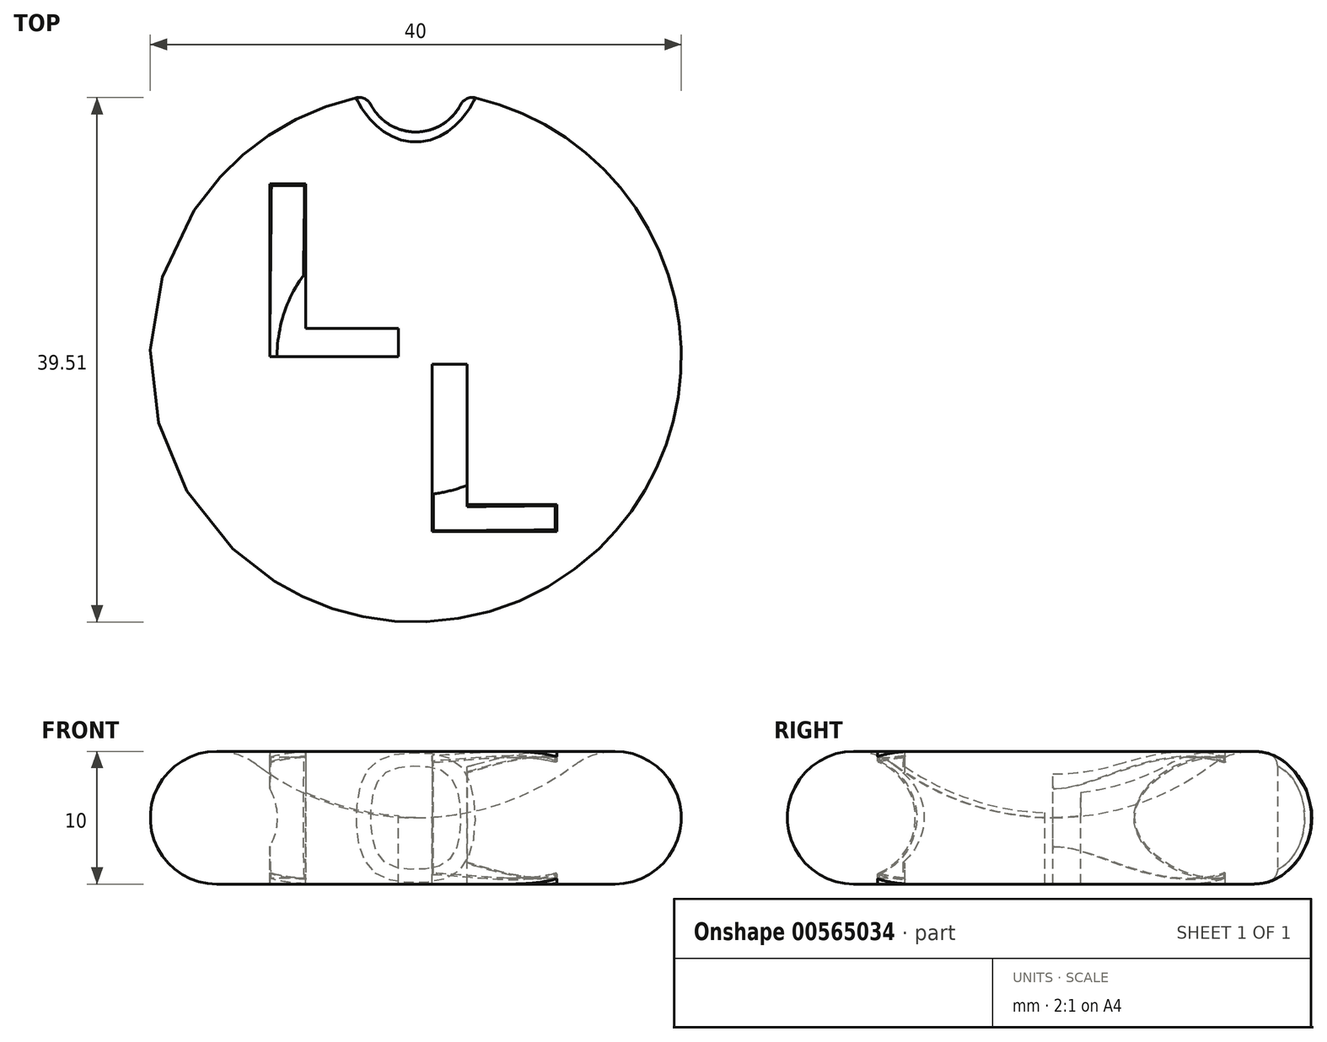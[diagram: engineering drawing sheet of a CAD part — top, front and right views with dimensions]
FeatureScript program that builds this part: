
annotation { "Feature Type Name" : "Feature", "Feature Type Description" : "" }
export const myFeature = defineFeature(function(context is Context, id is Id, definition is map)
    precondition{}
    {
        {
            var Q0;
            Q0=qCreatedBy(makeId("Front.planeOp"),FACE);
            var sketch = newSketch(context, id + "F0", { "sketchPlane" : qUnion([Q0])});
            skArc(sketch, "E0", {"start": v(-12, 9) * mm, "mid": v(-19.74, 6.58) * mm, "end": v(-15, 0) * mm});
            skArc(sketch, "E1", {"start": v(-12, 9) * mm, "mid": v(-6.32, 6.03) * mm, "end": v(0, 5) * mm});
            skLineSegment(sketch, "E2", {"start": v(0, 5) * mm, "end": v(0, 0) * mm});
            skLineSegment(sketch, "E3", {"start": v(0, 0) * mm, "end": v(-15, 0) * mm});
            skSolve(sketch);
        }
        {
            var Q0;
            Q0=makeQuery(id+"F0.imprint","IMPRINT",FACE,{"disambiguationData":[TD([[makeQuery(id+"F0.imprint","IMPRINT",EDGE,{"derivedFrom":sQuery(id+"F0.wireOp",EDGE,"E0")}),1.0]])]});
            var Q1;
            Q1=sQuery(id+"F0.wireOp",EDGE,"E2");
            revolve(context, id + "F1", {"entities" : qUnion([Q0]), "axis" : qUnion([Q1]), "revolveType" : RevolveType.FULL});
        }
        {
            var Q0;
            Q0=qCreatedBy(makeId("Top.planeOp"),FACE);
            cPlane(context, id + "F2", {"entities" : qUnion([Q0]), "cplaneType" : CPlaneType.OFFSET, "offset" : 10 * mm, "width" : 152.4 * mm, "height" : 152.4 * mm});
        }
        {
            var Q0;
            Q0=qCreatedBy(id+"F2.planeOp",FACE);
            var sketch = newSketch(context, id + "F3", { "sketchPlane" : qUnion([Q0])});
            skText(sketch, "E4", { "text": "L", "fontName": "Arimo-Bold.ttf"});
            skText(sketch, "E5", { "text": "L", "fontName": "Arimo-Bold.ttf"});
            const initialGuessF3  = {"E4": [-0.01226, 0, 1, 0, 0.0136], "E5": [0, -0.01319, 1, 0, 0.01319]};
            skSetInitialGuess(sketch, initialGuessF3);
            skSolve(sketch);
        }
        {
            var Q0;
            Q0=makeQuery(id+"F3.imprint","IMPRINT",FACE,{"disambiguationData":[TD([[makeQuery(id+"F3.imprint","IMPRINT",EDGE,{"derivedFrom":sQuery(id+"F3.wireOp",EDGE,"E5.sketch_text.stroke-0")}),-1.0]])]});
            var Q1;
            Q1=makeQuery(id+"F3.imprint","IMPRINT",FACE,{"disambiguationData":[TD([[makeQuery(id+"F3.imprint","IMPRINT",EDGE,{"derivedFrom":sQuery(id+"F3.wireOp",EDGE,"E4.sketch_text.stroke-0")}),-1.0]])]});
            extrude(context, id + "F4", {"entities" : qUnion([Q0, Q1]), "operationType" : NewBodyOperationType.REMOVE, "oppositeDirection" : true, "depth" : 25.4 * mm, "offsetDistance" : 25.4 * mm});
        }
        {
            var Q0;
            Q0=qCreatedBy(makeId("Front.planeOp"),FACE);
            var sketch = newSketch(context, id + "F5", { "sketchPlane" : qUnion([Q0])});
            skCircle(sketch, "E6", {"center": v(-15, 5) * mm, "radius": 4.56 * mm});
            skSolve(sketch);
        }
        {
            var Q0;
            Q0 = qSketchRegion(id + "F5", true);
            var Q1;
            Q1=sQuery(id+"F0.wireOp",EDGE,"E2");
            revolve(context, id + "F6", {"operationType" : NewBodyOperationType.ADD, "entities" : qUnion([Q0]), "axis" : qUnion([Q1]), "revolveType" : RevolveType.FULL});
        }
        {
            var Q0;
            Q0=qCreatedBy(makeId("Top.planeOp"),FACE);
            var sketch = newSketch(context, id + "F7", { "sketchPlane" : qUnion([Q0])});
            skCircle(sketch, "E7", {"center": v(0, 20.73) * mm, "radius": 3.8 * mm});
            skSolve(sketch);
        }
        {
            var Q0;
            Q0=makeQuery(id+"F7.imprint","IMPRINT",FACE,{"disambiguationData":[TD([[makeQuery(id+"F7.imprint","IMPRINT",EDGE,{"derivedFrom":sQuery(id+"F7.wireOp",EDGE,"E7")}),1.0]])]});
            extrude(context, id + "F8", {"entities" : qUnion([Q0]), "operationType" : NewBodyOperationType.REMOVE, "depth" : 25.4 * mm, "offsetDistance" : 25.4 * mm});
        }
        {
            var Q0;
            Q0=makeQuery(id+"F8.boolean.opBoolean","INTERSECT",EDGE,{"derivedFrom":[makeQuery(id+"F1.opRevolve","SWEPT_FACE",FACE,{"disambiguationData":[OSD([sQuery(id+"F0.wireOp",EDGE,"E0")])]}),makeQuery(id+"F8.opExtrude","SWEPT_FACE",FACE,{"disambiguationData":[OSD([sQuery(id+"F7.wireOp",EDGE,"E7")])]})]});
            fillet(context, id + "F9", {"entities" : qUnion([Q0]), "radius" : 1 * mm, "tangentPropagation" : true, "allowEdgeOverflow" : false});
        }
        {
            var Q0;
            Q0=makeQuery(id+"F6.boolean.opBoolean","INTERSECT",EDGE,{"disambiguationData":[OD(0.0)],"derivedFrom":[makeQuery(id+"F4.boolean.opBoolean","COPY",FACE,{"derivedFrom":makeQuery(id+"F4.opExtrude","SWEPT_FACE",FACE,{"disambiguationData":[OSD([sQuery(id+"F3.wireOp",EDGE,"E4.sketch_text.stroke-0")])]})}),makeQuery(id+"F6.opRevolve","SWEPT_FACE",FACE,{"disambiguationData":[OSD([sQuery(id+"F5.wireOp",EDGE,"E6")])]})]});
            var Q1;
            Q1=makeQuery(id+"F6.boolean.opBoolean","INTERSECT",EDGE,{"disambiguationData":[OD(1.0)],"derivedFrom":[makeQuery(id+"F4.boolean.opBoolean","COPY",FACE,{"derivedFrom":makeQuery(id+"F4.opExtrude","SWEPT_FACE",FACE,{"disambiguationData":[OSD([sQuery(id+"F3.wireOp",EDGE,"E5.sketch_text.stroke-5")])]})}),makeQuery(id+"F6.opRevolve","SWEPT_FACE",FACE,{"disambiguationData":[OSD([sQuery(id+"F5.wireOp",EDGE,"E6")])]})]});
            var Q2;
            Q2=makeQuery(id+"F6.boolean.opBoolean","INTERSECT",EDGE,{"disambiguationData":[OD(0.0)],"derivedFrom":[makeQuery(id+"F4.boolean.opBoolean","COPY",FACE,{"derivedFrom":makeQuery(id+"F4.opExtrude","SWEPT_FACE",FACE,{"disambiguationData":[OSD([sQuery(id+"F3.wireOp",EDGE,"E5.sketch_text.stroke-3")])]})}),makeQuery(id+"F6.opRevolve","SWEPT_FACE",FACE,{"disambiguationData":[OSD([sQuery(id+"F5.wireOp",EDGE,"E6")])]})]});
            var Q3;
            Q3=makeQuery(id+"F6.boolean.opBoolean","INTERSECT",EDGE,{"disambiguationData":[OD(0.0)],"derivedFrom":[makeQuery(id+"F4.boolean.opBoolean","COPY",FACE,{"derivedFrom":makeQuery(id+"F4.opExtrude","SWEPT_FACE",FACE,{"disambiguationData":[OSD([sQuery(id+"F3.wireOp",EDGE,"E5.sketch_text.stroke-4")])]})}),makeQuery(id+"F6.opRevolve","SWEPT_FACE",FACE,{"disambiguationData":[OSD([sQuery(id+"F5.wireOp",EDGE,"E6")])]})]});
            var Q4;
            Q4=makeQuery(id+"F6.boolean.opBoolean","INTERSECT",EDGE,{"disambiguationData":[OD(1.0)],"derivedFrom":[makeQuery(id+"F4.boolean.opBoolean","COPY",FACE,{"derivedFrom":makeQuery(id+"F4.opExtrude","SWEPT_FACE",FACE,{"disambiguationData":[OSD([sQuery(id+"F3.wireOp",EDGE,"E5.sketch_text.stroke-4")])]})}),makeQuery(id+"F6.opRevolve","SWEPT_FACE",FACE,{"disambiguationData":[OSD([sQuery(id+"F5.wireOp",EDGE,"E6")])]})]});
            var Q5;
            Q5=makeQuery(id+"F6.boolean.opBoolean","INTERSECT",EDGE,{"disambiguationData":[OD(1.0)],"derivedFrom":[makeQuery(id+"F4.boolean.opBoolean","COPY",FACE,{"derivedFrom":makeQuery(id+"F4.opExtrude","SWEPT_FACE",FACE,{"disambiguationData":[OSD([sQuery(id+"F3.wireOp",EDGE,"E5.sketch_text.stroke-3")])]})}),makeQuery(id+"F6.opRevolve","SWEPT_FACE",FACE,{"disambiguationData":[OSD([sQuery(id+"F5.wireOp",EDGE,"E6")])]})]});
            var Q6;
            Q6=makeQuery(id+"F6.boolean.opBoolean","INTERSECT",EDGE,{"disambiguationData":[OD(0.0)],"derivedFrom":[makeQuery(id+"F4.boolean.opBoolean","COPY",FACE,{"derivedFrom":makeQuery(id+"F4.opExtrude","SWEPT_FACE",FACE,{"disambiguationData":[OSD([sQuery(id+"F3.wireOp",EDGE,"E5.sketch_text.stroke-5")])]})}),makeQuery(id+"F6.opRevolve","SWEPT_FACE",FACE,{"disambiguationData":[OSD([sQuery(id+"F5.wireOp",EDGE,"E6")])]})]});
            var Q7;
            Q7=makeQuery(id+"F6.boolean.opBoolean","SPLIT",FACE,{"disambiguationData":[TD([makeQuery(id+"F4.boolean.opBoolean","COPY",FACE,{"derivedFrom":makeQuery(id+"F4.opExtrude","SWEPT_FACE",FACE,{"disambiguationData":[OSD([sQuery(id+"F3.wireOp",EDGE,"E4.sketch_text.stroke-0")])]})})])],"derivedFrom":makeQuery(id+"F6.opRevolve","SWEPT_FACE",FACE,{"disambiguationData":[OSD([sQuery(id+"F5.wireOp",EDGE,"E6")])]})});
            var Q8;
            Q8=makeQuery(id+"F6.boolean.opBoolean","INTERSECT",EDGE,{"derivedFrom":[makeQuery(id+"F4.boolean.opBoolean","COPY",FACE,{"derivedFrom":makeQuery(id+"F4.opExtrude","SWEPT_FACE",FACE,{"disambiguationData":[OSD([sQuery(id+"F3.wireOp",EDGE,"E5.sketch_text.stroke-0")])]})}),makeQuery(id+"F6.opRevolve","SWEPT_FACE",FACE,{"disambiguationData":[OSD([sQuery(id+"F5.wireOp",EDGE,"E6")])]})]});
            fillet(context, id + "F10", {"entities" : qUnion([Q0, Q1, Q2, Q3, Q4, Q5, Q6, Q7, Q8]), "radius" : .1 * mm, "tangentPropagation" : true, "allowEdgeOverflow" : false});
        }
    });
